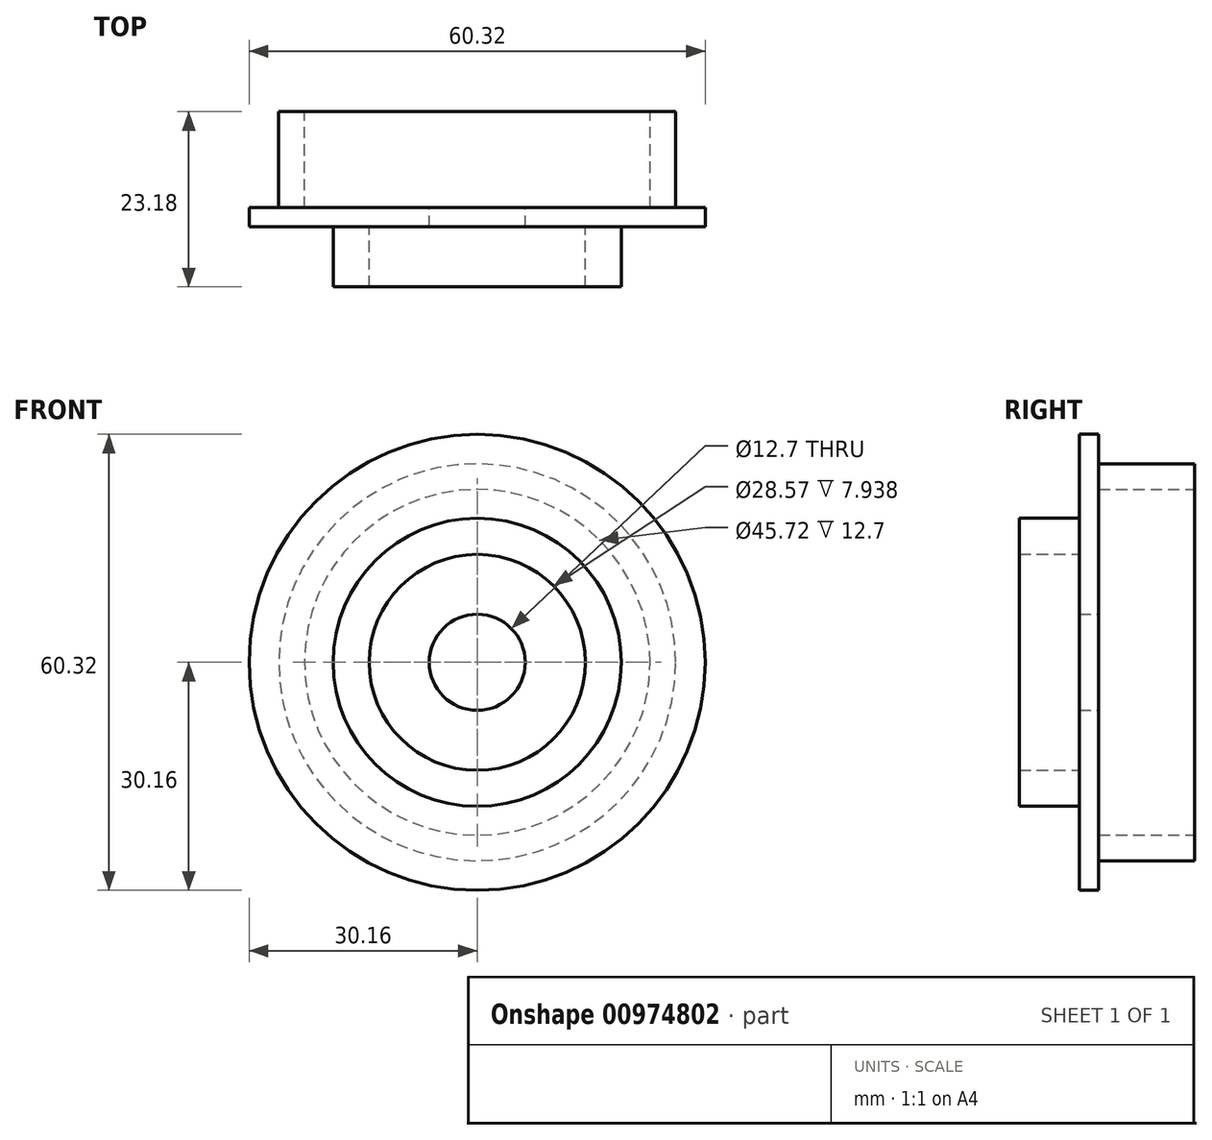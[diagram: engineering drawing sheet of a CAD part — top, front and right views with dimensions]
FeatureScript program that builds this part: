
annotation { "Feature Type Name" : "Feature", "Feature Type Description" : "" }
export const myFeature = defineFeature(function(context is Context, id is Id, definition is map)
    precondition{}
    {
        {
            var Q0;
            Q0=qCreatedBy(makeId("Front.planeOp"),FACE);
            var sketch = newSketch(context, id + "F0", { "sketchPlane" : qUnion([Q0])});
            skCircle(sketch, "E0", {"center": v(0, 0) * mm, "radius": 14.29 * mm});
            skCircle(sketch, "E1", {"center": v(0, 0) * mm, "radius": 19.05 * mm});
            skSolve(sketch);
        }
        {
            var Q0;
            Q0=makeQuery(id+"F0.imprint","IMPRINT",FACE,{"disambiguationData":[TD([[makeQuery(id+"F0.imprint","IMPRINT",EDGE,{"derivedFrom":sQuery(id+"F0.wireOp",EDGE,"E0")}),-1.0]])]});
            extrude(context, id + "F1", {"entities" : qUnion([Q0]), "depth" : 7.94 * mm, "offsetDistance" : 25.4 * mm});
        }
        {
            var Q0;
            Q0=makeQuery(id+"F1.opExtrude","CAP_FACE",FACE,{"disambiguationData":[OSD([sQuery(id+"F0.wireOp",EDGE,"E0"),sQuery(id+"F0.wireOp",EDGE,"E1")])],"isStart":true});
            var sketch = newSketch(context, id + "F2", { "sketchPlane" : qUnion([Q0])});
            skCircle(sketch, "E2", {"center": v(0, 0) * mm, "radius": 30.16 * mm});
            skSolve(sketch);
        }
        {
            var Q0;
            Q0 = qSketchRegion(id + "F2", true);
            extrude(context, id + "F3", {"entities" : qUnion([Q0]), "operationType" : NewBodyOperationType.ADD, "depth" : 15.24 * mm, "offsetDistance" : 25.4 * mm});
        }
        {
            var Q0;
            Q0=makeQuery(id+"F3.opExtrude","CAP_FACE",FACE,{"disambiguationData":[OSD([sQuery(id+"F2.wireOp",EDGE,"E2")])],"isStart":false});
            var sketch = newSketch(context, id + "F4", { "sketchPlane" : qUnion([Q0])});
            skCircle(sketch, "E3", {"center": v(0, 0) * mm, "radius": 6.35 * mm});
            skSolve(sketch);
        }
        {
            var Q0;
            Q0 = qSketchRegion(id + "F4", true);
            extrude(context, id + "F5", {"entities" : qUnion([Q0]), "operationType" : NewBodyOperationType.REMOVE, "endBound" : BoundingType.THROUGH_ALL, "oppositeDirection" : true, "depth" : 25.4 * mm, "offsetDistance" : 25.4 * mm});
        }
        {
            var Q0;
            Q0=makeQuery(id+"F3.opExtrude","CAP_FACE",FACE,{"disambiguationData":[OSD([sQuery(id+"F2.wireOp",EDGE,"E2")])],"isStart":false});
            var sketch = newSketch(context, id + "F6", { "sketchPlane" : qUnion([Q0])});
            skCircle(sketch, "E4", {"center": v(0, 0) * mm, "radius": 26.25 * mm});
            skCircle(sketch, "E5", {"center": v(0, 0) * mm, "radius": 32.39 * mm});
            skSolve(sketch);
        }
        {
            var Q0;
            Q0 = qSketchRegion(id + "F6", true);
            extrude(context, id + "F7", {"entities" : qUnion([Q0]), "operationType" : NewBodyOperationType.REMOVE, "oppositeDirection" : true, "depth" : 12.7 * mm, "offsetDistance" : 25.4 * mm});
        }
        {
            var Q0;
            Q0=makeQuery(id+"F3.opExtrude","CAP_FACE",FACE,{"disambiguationData":[OSD([sQuery(id+"F2.wireOp",EDGE,"E2")])],"isStart":false});
            var sketch = newSketch(context, id + "F8", { "sketchPlane" : qUnion([Q0])});
            skCircle(sketch, "E6", {"center": v(0, 0) * mm, "radius": 22.86 * mm});
            skSolve(sketch);
        }
        {
            var Q0;
            Q0=makeQuery(id+"F8.imprint","IMPRINT",FACE,{"disambiguationData":[TD([[makeQuery(id+"F8.imprint","IMPRINT",EDGE,{"derivedFrom":sQuery(id+"F8.wireOp",EDGE,"E6")}),1.0]])]});
            extrude(context, id + "F9", {"entities" : qUnion([Q0]), "operationType" : NewBodyOperationType.REMOVE, "oppositeDirection" : true, "depth" : 12.7 * mm, "offsetDistance" : 25.4 * mm});
        }
    });
